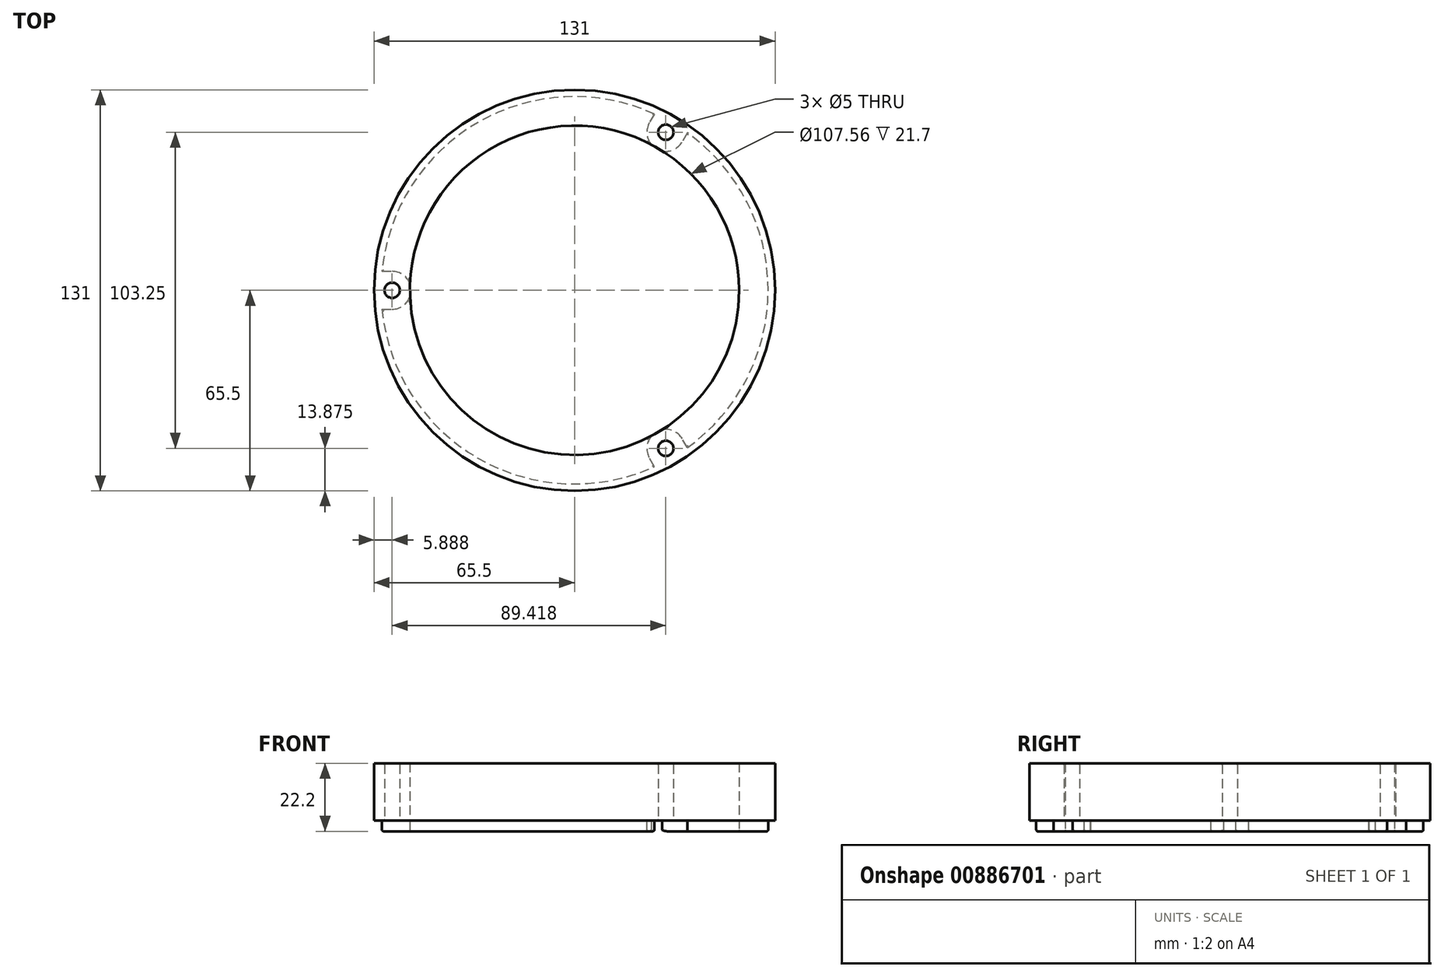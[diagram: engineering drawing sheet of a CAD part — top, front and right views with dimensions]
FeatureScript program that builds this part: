
annotation { "Feature Type Name" : "Feature", "Feature Type Description" : "" }
export const myFeature = defineFeature(function(context is Context, id is Id, definition is map)
    precondition{}
    {
        {
            var Q0;
            Q0=qCreatedBy(makeId("Top.planeOp"),FACE);
            var sketch = newSketch(context, id + "F0", { "sketchPlane" : qUnion([Q0])});
            skCircle(sketch, "E0", {"center": v(0, 0) * mm, "radius": 65.5 * mm});
            skCircle(sketch, "E1", {"center": v(0, 0) * mm, "radius": 53.78 * mm});
            skArc(sketch, "E2", {"start": v(-59.61, -6.2) * mm, "mid": v(-53.41, 0) * mm, "end": v(-59.61, 6.2) * mm});
            skLineSegment(sketch, "E3", {"start": v(-65.2, 6.2) * mm, "end": v(-59.61, 6.2) * mm});
            skLineSegment(sketch, "E4", {"start": v(-65.2, -6.2) * mm, "end": v(-59.61, -6.2) * mm});
            skCircle(sketch, "E5", {"center": v(-59.61, 0) * mm, "radius": 2.5 * mm});
            skArc(sketch, "E6.1.0", {"start": v(35.18, -48.53) * mm, "mid": v(26.7, -46.26) * mm, "end": v(24.44, -54.73) * mm});
            skLineSegment(sketch, "E6.1.1", {"start": v(37.97, -53.37) * mm, "end": v(35.18, -48.53) * mm});
            skCircle(sketch, "E6.1.2", {"center": v(29.8, -51.63) * mm, "radius": 2.5 * mm});
            skLineSegment(sketch, "E6.1.3", {"start": v(27.23, -59.57) * mm, "end": v(24.44, -54.73) * mm});
            skArc(sketch, "E6.2.0", {"start": v(24.44, 54.73) * mm, "mid": v(26.7, 46.26) * mm, "end": v(35.18, 48.53) * mm});
            skLineSegment(sketch, "E6.2.1", {"start": v(27.23, 59.57) * mm, "end": v(24.44, 54.73) * mm});
            skCircle(sketch, "E6.2.2", {"center": v(29.8, 51.63) * mm, "radius": 2.5 * mm});
            skLineSegment(sketch, "E6.2.3", {"start": v(37.97, 53.37) * mm, "end": v(35.18, 48.53) * mm});
            skArc(sketch, "E7", {"start": v(36.84, -51.41) * mm, "mid": v(63.25, 0) * mm, "end": v(36.84, 51.41) * mm});
            skArc(sketch, "E8.trimOffspring", {"start": v(-62.95, -6.2) * mm, "mid": v(-31.62, -54.78) * mm, "end": v(26.1, -57.61) * mm});
            skArc(sketch, "E9.trimOffspring", {"start": v(26.1, 57.61) * mm, "mid": v(-31.62, 54.78) * mm, "end": v(-62.95, 6.2) * mm});
            skLineSegment(sketch, "E10", {"start": v(0, 0) * mm, "end": v(-65.5, 0) * mm, "construction": true});
            skSolve(sketch);
        }
        {
            var Q0;
            {var subQ0=sQuery(id+"F0.wireOp",EDGE,"E3");Q0=makeQuery(id+"F0.imprint","IMPRINT",FACE,{"disambiguationData":[TD([[makeQuery(id+"F0.imprint","IMPRINT",EDGE,{"derivedFrom":subQ0}),1.0]])]});}
            var Q1;
            {var subQ0=sQuery(id+"F0.wireOp",EDGE,"E3");Q1=makeQuery(id+"F0.imprint","IMPRINT",FACE,{"disambiguationData":[TD([[makeQuery(id+"F0.imprint","IMPRINT",EDGE,{"derivedFrom":subQ0}),-1.0]])]});}
            var Q2;
            {var subQ0=sQuery(id+"F0.wireOp",EDGE,"E4");Q2=makeQuery(id+"F0.imprint","IMPRINT",FACE,{"disambiguationData":[TD([[makeQuery(id+"F0.imprint","IMPRINT",EDGE,{"derivedFrom":subQ0}),-1.0]])]});}
            var Q3;
            {var subQ0=sQuery(id+"F0.wireOp",EDGE,"E6.1.1");Q3=makeQuery(id+"F0.imprint","IMPRINT",FACE,{"disambiguationData":[TD([[makeQuery(id+"F0.imprint","IMPRINT",EDGE,{"derivedFrom":subQ0}),1.0]])]});}
            var Q4;
            {var subQ0=sQuery(id+"F0.wireOp",EDGE,"E6.1.1");Q4=makeQuery(id+"F0.imprint","IMPRINT",FACE,{"disambiguationData":[TD([[makeQuery(id+"F0.imprint","IMPRINT",EDGE,{"derivedFrom":subQ0}),-1.0]])]});}
            var Q5;
            {var subQ0=sQuery(id+"F0.wireOp",EDGE,"E6.2.1");Q5=makeQuery(id+"F0.imprint","IMPRINT",FACE,{"disambiguationData":[TD([[makeQuery(id+"F0.imprint","IMPRINT",EDGE,{"derivedFrom":subQ0}),1.0]])]});}
            var Q6;
            {var subQ3=sQuery(id+"F0.wireOp",EDGE,"E7");Q6=makeQuery(id+"F0.imprint","IMPRINT",FACE,{"disambiguationData":[TD([[makeQuery(id+"F0.imprint","IMPRINT",EDGE,{"derivedFrom":subQ3}),1.0]])]});}
            var Q7;
            {var subQ3=sQuery(id+"F0.wireOp",EDGE,"E8.trimOffspring");Q7=makeQuery(id+"F0.imprint","IMPRINT",FACE,{"disambiguationData":[TD([[makeQuery(id+"F0.imprint","IMPRINT",EDGE,{"derivedFrom":subQ3}),1.0]])]});}
            var Q8;
            {var subQ8=sQuery(id+"F0.wireOp",EDGE,"E9.trimOffspring");Q8=makeQuery(id+"F0.imprint","IMPRINT",FACE,{"disambiguationData":[TD([[makeQuery(id+"F0.imprint","IMPRINT",EDGE,{"derivedFrom":subQ8}),1.0]])]});}
            extrude(context, id + "F1", {"entities" : qUnion([Q0, Q1, Q2, Q3, Q4, Q5, Q6, Q7, Q8]), "depth" : 18.75 * mm, "offsetDistance" : 25 * mm});
        }
        {
            var Q0;
            {var subQ3=sQuery(id+"F0.wireOp",EDGE,"E8.trimOffspring");Q0=makeQuery(id+"F0.imprint","IMPRINT",FACE,{"disambiguationData":[TD([[makeQuery(id+"F0.imprint","IMPRINT",EDGE,{"derivedFrom":subQ3}),1.0]])]});}
            var Q1;
            {var subQ3=sQuery(id+"F0.wireOp",EDGE,"E7");Q1=makeQuery(id+"F0.imprint","IMPRINT",FACE,{"disambiguationData":[TD([[makeQuery(id+"F0.imprint","IMPRINT",EDGE,{"derivedFrom":subQ3}),1.0]])]});}
            var Q2;
            {var subQ8=sQuery(id+"F0.wireOp",EDGE,"E9.trimOffspring");Q2=makeQuery(id+"F0.imprint","IMPRINT",FACE,{"disambiguationData":[TD([[makeQuery(id+"F0.imprint","IMPRINT",EDGE,{"derivedFrom":subQ8}),1.0]])]});}
            extrude(context, id + "F2", {"entities" : qUnion([Q0, Q1, Q2]), "operationType" : NewBodyOperationType.ADD, "depth" : -3.45 * mm, "offsetDistance" : 25 * mm});
        }
        {
            var Q0;
            Q0=makeQuery(id+"F1.opExtrude","CAP_EDGE",EDGE,{"disambiguationData":[OSD([sQuery(id+"F0.wireOp",EDGE,"E5")])],"isStart":true});
            var Q1;
            Q1=makeQuery(id+"F1.opExtrude","CAP_EDGE",EDGE,{"disambiguationData":[OSD([sQuery(id+"F0.wireOp",EDGE,"E6.2.2")])],"isStart":true});
            var Q2;
            Q2=makeQuery(id+"F1.opExtrude","CAP_EDGE",EDGE,{"disambiguationData":[OSD([sQuery(id+"F0.wireOp",EDGE,"E6.1.2")])],"isStart":true});
            var Q3;
            Q3=makeQuery(id+"F1.opExtrude","CAP_EDGE",EDGE,{"disambiguationData":[OSD([sQuery(id+"F0.wireOp",EDGE,"E6.2.2")])],"isStart":false});
            var Q4;
            Q4=makeQuery(id+"F1.opExtrude","CAP_EDGE",EDGE,{"disambiguationData":[OSD([sQuery(id+"F0.wireOp",EDGE,"E6.1.2")])],"isStart":false});
            var Q5;
            Q5=makeQuery(id+"F1.opExtrude","CAP_EDGE",EDGE,{"disambiguationData":[OSD([sQuery(id+"F0.wireOp",EDGE,"E5")])],"isStart":false});
            var Q6;
            Q6=makeQuery(id+"F2.opExtrude","CAP_EDGE",EDGE,{"disambiguationData":[OSD([sQuery(id+"F0.wireOp",EDGE,"E4")])],"isStart":false});
            var Q7;
            {var subQ0=sQuery(id+"F0.wireOp",EDGE,"E2");Q7=makeQuery(id+"F2.opExtrude","CAP_EDGE",EDGE,{"disambiguationData":[OSD([subQ0]),TDD([makeQuery(id+"F0.imprint","IMPRINT",EDGE,{"disambiguationData":[TD([[makeQuery(id+"F0.imprint","INTERSECT",VERTEX,{"derivedFrom":[subQ0,sQuery(id+"F0.wireOp",EDGE,"E4")]}),-1.0]])],"derivedFrom":subQ0})])],"isStart":false});}
            var Q8;
            {var subQ0=sQuery(id+"F0.wireOp",EDGE,"E2");Q8=makeQuery(id+"F2.opExtrude","CAP_EDGE",EDGE,{"disambiguationData":[OSD([subQ0]),TDD([makeQuery(id+"F0.imprint","IMPRINT",EDGE,{"disambiguationData":[TD([[makeQuery(id+"F0.imprint","INTERSECT",VERTEX,{"derivedFrom":[subQ0,sQuery(id+"F0.wireOp",EDGE,"E3")]}),1.0]])],"derivedFrom":subQ0})])],"isStart":false});}
            var Q9;
            Q9=makeQuery(id+"F2.opExtrude","CAP_EDGE",EDGE,{"disambiguationData":[OSD([sQuery(id+"F0.wireOp",EDGE,"E3")])],"isStart":false});
            var Q10;
            {var subQ0=sQuery(id+"F0.wireOp",EDGE,"E6.2.0");Q10=makeQuery(id+"F2.opExtrude","CAP_EDGE",EDGE,{"disambiguationData":[OSD([subQ0]),TDD([makeQuery(id+"F0.imprint","IMPRINT",EDGE,{"disambiguationData":[TD([[makeQuery(id+"F0.imprint","INTERSECT",VERTEX,{"derivedFrom":[subQ0,sQuery(id+"F0.wireOp",EDGE,"E6.2.3")]}),1.0]])],"derivedFrom":subQ0})])],"isStart":false});}
            var Q11;
            Q11=makeQuery(id+"F2.opExtrude","CAP_EDGE",EDGE,{"disambiguationData":[OSD([sQuery(id+"F0.wireOp",EDGE,"E6.2.3")])],"isStart":false});
            var Q12;
            {var subQ0=sQuery(id+"F0.wireOp",EDGE,"E6.2.0");Q12=makeQuery(id+"F2.opExtrude","CAP_EDGE",EDGE,{"disambiguationData":[OSD([subQ0]),TDD([makeQuery(id+"F0.imprint","IMPRINT",EDGE,{"disambiguationData":[TD([[makeQuery(id+"F0.imprint","INTERSECT",VERTEX,{"derivedFrom":[subQ0,sQuery(id+"F0.wireOp",EDGE,"E6.2.1")]}),-1.0]])],"derivedFrom":subQ0})])],"isStart":false});}
            var Q13;
            Q13=makeQuery(id+"F2.opExtrude","CAP_EDGE",EDGE,{"disambiguationData":[OSD([sQuery(id+"F0.wireOp",EDGE,"E6.2.1")])],"isStart":false});
            var Q14;
            Q14=makeQuery(id+"F2.opExtrude","CAP_EDGE",EDGE,{"disambiguationData":[OSD([sQuery(id+"F0.wireOp",EDGE,"E6.1.1")])],"isStart":false});
            var Q15;
            {var subQ0=sQuery(id+"F0.wireOp",EDGE,"E6.1.0");Q15=makeQuery(id+"F2.opExtrude","CAP_EDGE",EDGE,{"disambiguationData":[OSD([subQ0]),TDD([makeQuery(id+"F0.imprint","IMPRINT",EDGE,{"disambiguationData":[TD([[makeQuery(id+"F0.imprint","INTERSECT",VERTEX,{"derivedFrom":[subQ0,sQuery(id+"F0.wireOp",EDGE,"E6.1.1")]}),-1.0]])],"derivedFrom":subQ0})])],"isStart":false});}
            var Q16;
            {var subQ0=sQuery(id+"F0.wireOp",EDGE,"E6.1.0");Q16=makeQuery(id+"F2.opExtrude","CAP_EDGE",EDGE,{"disambiguationData":[OSD([subQ0]),TDD([makeQuery(id+"F0.imprint","IMPRINT",EDGE,{"disambiguationData":[TD([[makeQuery(id+"F0.imprint","INTERSECT",VERTEX,{"derivedFrom":[subQ0,sQuery(id+"F0.wireOp",EDGE,"E6.1.3")]}),1.0]])],"derivedFrom":subQ0})])],"isStart":false});}
            var Q17;
            Q17=makeQuery(id+"F2.opExtrude","CAP_EDGE",EDGE,{"disambiguationData":[OSD([sQuery(id+"F0.wireOp",EDGE,"E6.1.3")])],"isStart":false});
            var Q18;
            {var subQ0=sQuery(id+"F0.wireOp",EDGE,"E1");Q18=makeQuery(id+"F2.opExtrude","CAP_EDGE",EDGE,{"disambiguationData":[OSD([subQ0]),TDD([makeQuery(id+"F0.imprint","IMPRINT",EDGE,{"disambiguationData":[TD([[makeQuery(id+"F0.imprint","INTERSECT",VERTEX,{"disambiguationData":[OD(1.0)],"derivedFrom":[subQ0,sQuery(id+"F0.wireOp",EDGE,"E6.2.0")]}),1.0]])],"derivedFrom":subQ0})])],"isStart":false});}
            var Q19;
            {var subQ0=sQuery(id+"F0.wireOp",EDGE,"E1");Q19=makeQuery(id+"F2.opExtrude","CAP_EDGE",EDGE,{"disambiguationData":[OSD([subQ0]),TDD([makeQuery(id+"F0.imprint","IMPRINT",EDGE,{"disambiguationData":[TD([[makeQuery(id+"F0.imprint","INTERSECT",VERTEX,{"disambiguationData":[OD(1.0)],"derivedFrom":[subQ0,sQuery(id+"F0.wireOp",EDGE,"E2")]}),-1.0]])],"derivedFrom":subQ0})])],"isStart":false});}
            var Q20;
            {var subQ0=sQuery(id+"F0.wireOp",EDGE,"E1");Q20=makeQuery(id+"F2.opExtrude","CAP_EDGE",EDGE,{"disambiguationData":[OSD([subQ0]),TDD([makeQuery(id+"F0.imprint","IMPRINT",EDGE,{"disambiguationData":[TD([[makeQuery(id+"F0.imprint","INTERSECT",VERTEX,{"disambiguationData":[OD(0.0)],"derivedFrom":[subQ0,sQuery(id+"F0.wireOp",EDGE,"E6.2.0")]}),-1.0]])],"derivedFrom":subQ0})])],"isStart":false});}
            var Q21;
            Q21=makeQuery(id+"F2.opExtrude","CAP_EDGE",EDGE,{"disambiguationData":[OSD([sQuery(id+"F0.wireOp",EDGE,"E7")])],"isStart":false});
            var Q22;
            Q22=makeQuery(id+"F2.opExtrude","CAP_EDGE",EDGE,{"disambiguationData":[OSD([sQuery(id+"F0.wireOp",EDGE,"E8.trimOffspring")])],"isStart":false});
            var Q23;
            Q23=makeQuery(id+"F2.opExtrude","CAP_EDGE",EDGE,{"disambiguationData":[OSD([sQuery(id+"F0.wireOp",EDGE,"E9.trimOffspring")])],"isStart":false});
            fillet(context, id + "F3", {"entities" : qUnion([Q0, Q1, Q2, Q3, Q4, Q5, Q6, Q7, Q8, Q9, Q10, Q11, Q12, Q13, Q14, Q15, Q16, Q17, Q18, Q19, Q20, Q21, Q22, Q23]), "radius" : 0.5 * mm, "tangentPropagation" : true, "allowEdgeOverflow" : false});
        }
    });
